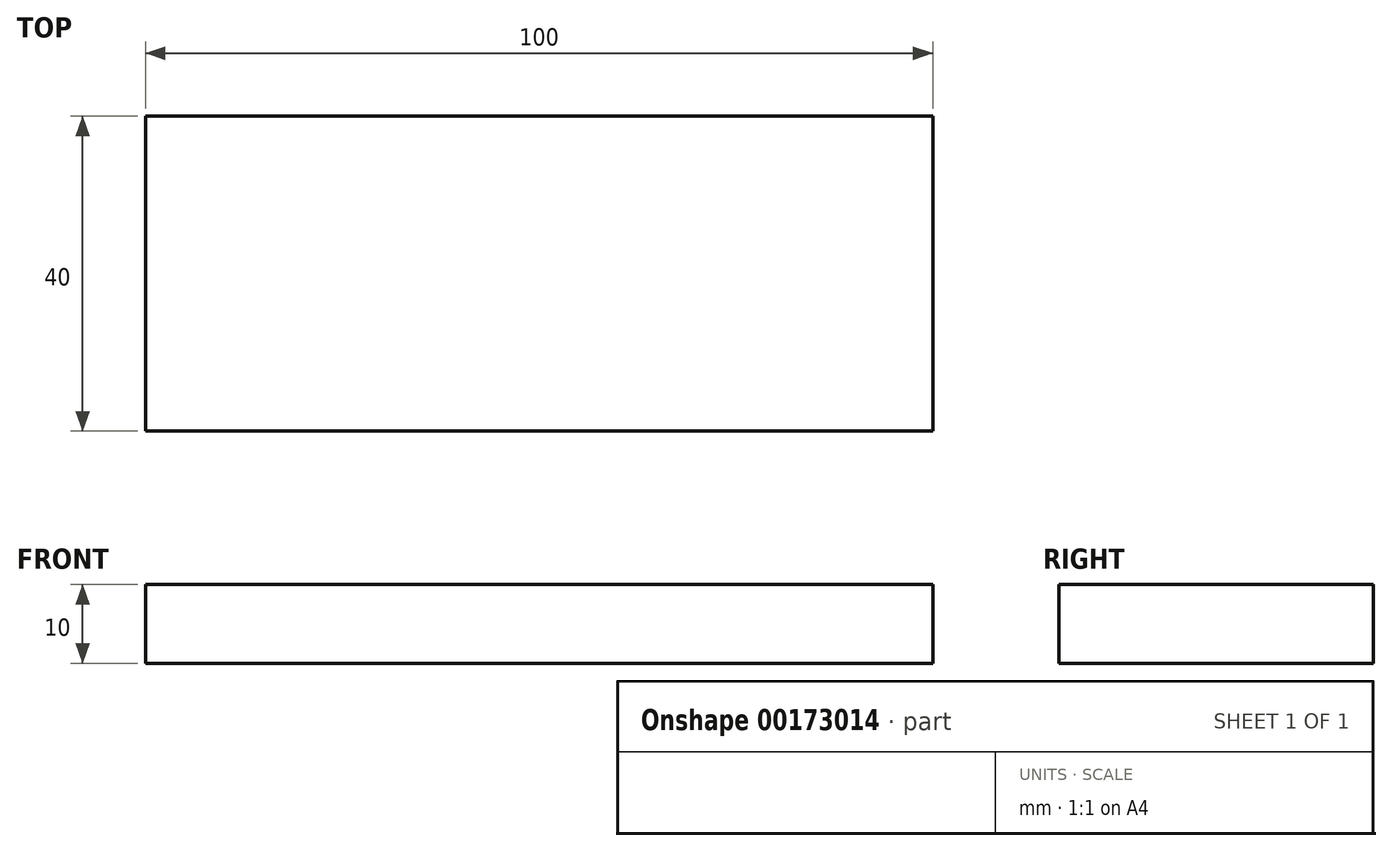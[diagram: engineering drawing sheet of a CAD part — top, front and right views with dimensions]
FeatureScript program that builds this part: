
annotation { "Feature Type Name" : "Feature", "Feature Type Description" : "" }
export const myFeature = defineFeature(function(context is Context, id is Id, definition is map)
    precondition{}
    {
        {
            var Q0;
            Q0=qCreatedBy(makeId("Top.planeOp"),FACE);
            var sketch = newSketch(context, id + "F0", { "sketchPlane" : qUnion([Q0])});
            skLineSegment(sketch, "E0.bottom", {"start": v(50, -20) * mm, "end": v(-50, -20) * mm});
            skLineSegment(sketch, "E0.top", {"start": v(50, 20) * mm, "end": v(-50, 20) * mm});
            skLineSegment(sketch, "E0.left", {"start": v(50, -20) * mm, "end": v(50, 20) * mm});
            skLineSegment(sketch, "E0.right", {"start": v(-50, -20) * mm, "end": v(-50, 20) * mm});
            skPoint(sketch, "E0.middle", {"position": v(0, 0) * mm});
            skSolve(sketch);
        }
        {
            var Q0;
            Q0 = qSketchRegion(id + "F0", true);
            extrude(context, id + "F1", {"entities" : qUnion([Q0]), "depth" : 10 * mm});
        }
    });
